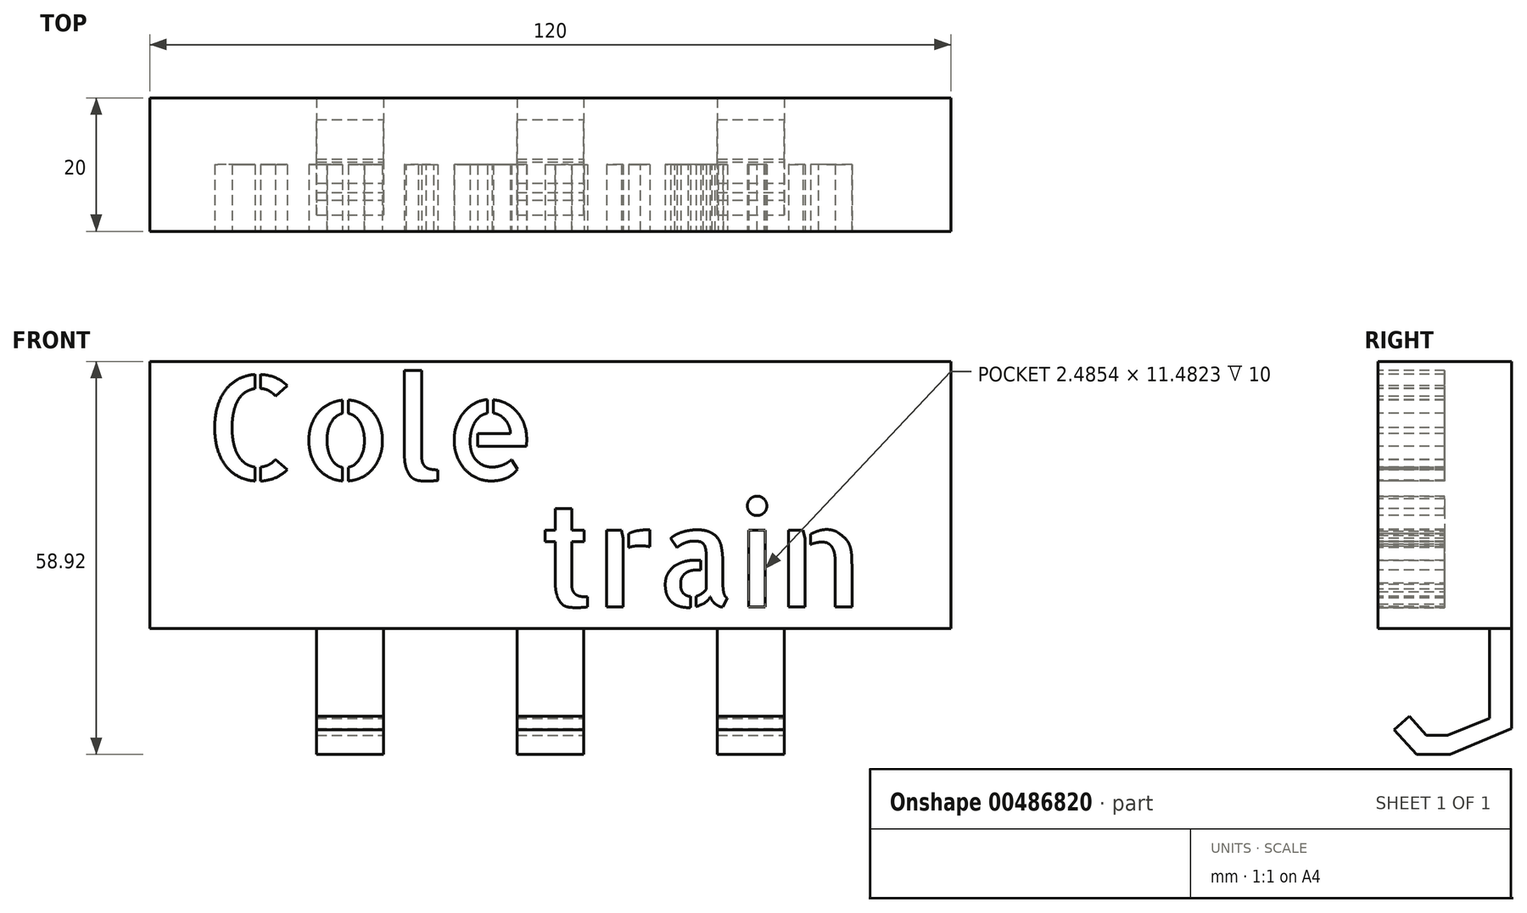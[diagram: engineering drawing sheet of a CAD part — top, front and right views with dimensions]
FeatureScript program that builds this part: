
annotation { "Feature Type Name" : "Feature", "Feature Type Description" : "" }
export const myFeature = defineFeature(function(context is Context, id is Id, definition is map)
    precondition{}
    {
        {
            var Q0;
            Q0=qCreatedBy(makeId("Front.planeOp"),FACE);
            var sketch = newSketch(context, id + "F0", { "sketchPlane" : qUnion([Q0])});
            skLineSegment(sketch, "E0", {"start": v(0, 0) * mm, "end": v(120, 0) * mm});
            skLineSegment(sketch, "E1", {"start": v(120, 0) * mm, "end": v(120, 40) * mm});
            skLineSegment(sketch, "E2", {"start": v(120, 40) * mm, "end": v(0, 40) * mm});
            skLineSegment(sketch, "E3", {"start": v(0, 40) * mm, "end": v(0, 0) * mm});
            skSolve(sketch);
        }
        {
            var Q0;
            Q0=makeQuery(id+"F0.imprint","IMPRINT",FACE,{"disambiguationData":[TD([[makeQuery(id+"F0.imprint","IMPRINT",EDGE,{"derivedFrom":sQuery(id+"F0.wireOp",EDGE,"E0")}),1.0]])]});
            extrude(context, id + "F1", {"entities" : qUnion([Q0]), "depth" : 20 * mm});
        }
        {
            var Q0;
            Q0=makeQuery(id+"FDrX07v6x76nU2d_1.boolean.opBoolean","MERGE",FACE,{"derivedFrom":[makeQuery(id+"F1.opExtrude","SWEPT_FACE",FACE,{"disambiguationData":[OSD([sQuery(id+"F0.wireOp",EDGE,"E3")])]}),makeQuery(id+"FDrX07v6x76nU2d_1.opExtrude","CAP_FACE",FACE,{"disambiguationData":[OSD([sQuery(id+"FK7LQfFWzsV9AYp_1.wireOp",EDGE,"OMKRaW7R-vSLb-FYLp-IFkI-dfkIP6oVdDYg"),sQuery(id+"FK7LQfFWzsV9AYp_1.wireOp",EDGE,"lYjhFyQz-pdgc-lFaZ-xAnS-GeXkMmyUxUMK"),sQuery(id+"FK7LQfFWzsV9AYp_1.wireOp",EDGE,"zUAezEfJ-fcOu-USHg-nBjk-tvtQ3sMSXvug"),sQuery(id+"FK7LQfFWzsV9AYp_1.wireOp",EDGE,"2Er81OVU-9qJa-L23g-iBGc-yoonpNpwCUbS"),sQuery(id+"FK7LQfFWzsV9AYp_1.wireOp",EDGE,"PpuGXbKU-hLP1-UUbL-IeXQ-y96dniKJ76El"),sQuery(id+"FK7LQfFWzsV9AYp_1.wireOp",EDGE,"mb6oPqYD-JF6T-TfRG-1Bwp-kSzYiZRObz3x"),sQuery(id+"FK7LQfFWzsV9AYp_1.wireOp",EDGE,"EnuxGocE-ggdU-0ooB-hZ5K-RwG9sS1lhak2"),sQuery(id+"FK7LQfFWzsV9AYp_1.wireOp",EDGE,"iuQDp4Cp-PRgE-UXjH-uZSU-5Cy1tqOp6oE6"),sQuery(id+"FK7LQfFWzsV9AYp_1.wireOp",EDGE,"NXjEv2nQ-JPso-gn4P-wQue-BciRGQNFK3fX"),sQuery(id+"FK7LQfFWzsV9AYp_1.wireOp",EDGE,"TtK5KWP1-CATt-S2zs-VjLP-lxPlcXjjFvsI")])],"isStart":true})]});
            cPlane(context, id + "F2", {"entities" : qUnion([Q0]), "cplaneType" : CPlaneType.OFFSET, "offset" : 30 * mm, "oppositeDirection" : true, "width" : 150 * mm, "height" : 150 * mm});
        }
        {
            var Q0;
            Q0=qCreatedBy(id+"F2.planeOp",FACE);
            var sketch = newSketch(context, id + "F3", { "sketchPlane" : qUnion([Q0])});
            skLineSegment(sketch, "E4.0.0", {"start": v(0, 40) * mm, "end": v(0, -15) * mm});
            skLineSegment(sketch, "E4.0.1", {"start": v(0, -15) * mm, "end": v(9.2, -18.92) * mm});
            skLineSegment(sketch, "E4.0.2", {"start": v(9.2, -18.92) * mm, "end": v(14.2, -18.92) * mm});
            skLineSegment(sketch, "E4.0.3", {"start": v(14.2, -18.92) * mm, "end": v(17.55, -15.21) * mm});
            skLineSegment(sketch, "E4.0.4", {"start": v(17.55, -15.21) * mm, "end": v(15.33, -13.2) * mm});
            skLineSegment(sketch, "E4.0.5", {"start": v(15.33, -13.2) * mm, "end": v(12.77, -16.03) * mm});
            skLineSegment(sketch, "E4.0.6", {"start": v(12.77, -16.03) * mm, "end": v(9.6, -16.03) * mm});
            skLineSegment(sketch, "E4.0.7", {"start": v(9.6, -16.03) * mm, "end": v(3.27, -13.5) * mm});
            skLineSegment(sketch, "E4.0.8", {"start": v(3.27, -13.5) * mm, "end": v(3.27, 0) * mm});
            skLineSegment(sketch, "E4.0.9", {"start": v(3.27, 0) * mm, "end": v(20, 0) * mm});
            skLineSegment(sketch, "E4.0.10", {"start": v(20, 0) * mm, "end": v(20, 40) * mm});
            skLineSegment(sketch, "E4.0.11", {"start": v(20, 40) * mm, "end": v(0, 40) * mm});
            skSolve(sketch);
        }
        {
            var Q0;
            Q0=makeQuery(id+"F3.imprint","IMPRINT",FACE,{"disambiguationData":[TD([[makeQuery(id+"F3.imprint","IMPRINT",EDGE,{"derivedFrom":sQuery(id+"F3.wireOp",EDGE,"E4.0.0")}),1.0]])]});
            extrude(context, id + "F4", {"entities" : qUnion([Q0]), "operationType" : NewBodyOperationType.ADD, "endBound" : BoundingType.SYMMETRIC, "depth" : 10 * mm});
        }
        {
            var Q0;
            Q0=qCreatedBy(id+"F2.planeOp",FACE);
            cPlane(context, id + "F5", {"entities" : qUnion([Q0]), "cplaneType" : CPlaneType.OFFSET, "offset" : 30 * mm, "oppositeDirection" : true, "width" : 150 * mm, "height" : 150 * mm});
        }
        {
            var Q0;
            Q0=qCreatedBy(id+"F5.planeOp",FACE);
            var sketch = newSketch(context, id + "F6", { "sketchPlane" : qUnion([Q0])});
            skLineSegment(sketch, "E5.0.0", {"start": v(0, 40) * mm, "end": v(0, -15) * mm});
            skLineSegment(sketch, "E5.0.1", {"start": v(0, -15) * mm, "end": v(9.2, -18.92) * mm});
            skLineSegment(sketch, "E5.0.2", {"start": v(9.2, -18.92) * mm, "end": v(14.2, -18.92) * mm});
            skLineSegment(sketch, "E5.0.3", {"start": v(14.2, -18.92) * mm, "end": v(17.55, -15.21) * mm});
            skLineSegment(sketch, "E5.0.4", {"start": v(17.55, -15.21) * mm, "end": v(15.33, -13.2) * mm});
            skLineSegment(sketch, "E5.0.5", {"start": v(15.33, -13.2) * mm, "end": v(12.77, -16.03) * mm});
            skLineSegment(sketch, "E5.0.6", {"start": v(12.77, -16.03) * mm, "end": v(9.6, -16.03) * mm});
            skLineSegment(sketch, "E5.0.7", {"start": v(9.6, -16.03) * mm, "end": v(3.27, -13.5) * mm});
            skLineSegment(sketch, "E5.0.8", {"start": v(3.27, -13.5) * mm, "end": v(3.27, 0) * mm});
            skLineSegment(sketch, "E5.0.9", {"start": v(3.27, 0) * mm, "end": v(20, 0) * mm});
            skLineSegment(sketch, "E5.0.10", {"start": v(20, 0) * mm, "end": v(20, 40) * mm});
            skLineSegment(sketch, "E5.0.11", {"start": v(20, 40) * mm, "end": v(0, 40) * mm});
            skSolve(sketch);
        }
        {
            var Q0;
            Q0 = qSketchRegion(id + "F6", true);
            extrude(context, id + "F7", {"entities" : qUnion([Q0]), "operationType" : NewBodyOperationType.ADD, "endBound" : BoundingType.SYMMETRIC, "depth" : 10 * mm});
        }
        {
            var Q0;
            Q0=qCreatedBy(id+"F5.planeOp",FACE);
            cPlane(context, id + "F8", {"entities" : qUnion([Q0]), "cplaneType" : CPlaneType.OFFSET, "offset" : 30 * mm, "oppositeDirection" : true, "width" : 150 * mm, "height" : 150 * mm});
        }
        {
            var Q0;
            Q0=qCreatedBy(id+"F8.planeOp",FACE);
            var sketch = newSketch(context, id + "F9", { "sketchPlane" : qUnion([Q0])});
            skLineSegment(sketch, "E6.0.0", {"start": v(0, 40) * mm, "end": v(0, -15) * mm});
            skLineSegment(sketch, "E6.0.1", {"start": v(0, -15) * mm, "end": v(9.2, -18.92) * mm});
            skLineSegment(sketch, "E6.0.2", {"start": v(9.2, -18.92) * mm, "end": v(14.2, -18.92) * mm});
            skLineSegment(sketch, "E6.0.3", {"start": v(14.2, -18.92) * mm, "end": v(17.55, -15.21) * mm});
            skLineSegment(sketch, "E6.0.4", {"start": v(17.55, -15.21) * mm, "end": v(15.33, -13.2) * mm});
            skLineSegment(sketch, "E6.0.5", {"start": v(15.33, -13.2) * mm, "end": v(12.77, -16.03) * mm});
            skLineSegment(sketch, "E6.0.6", {"start": v(12.77, -16.03) * mm, "end": v(9.6, -16.03) * mm});
            skLineSegment(sketch, "E6.0.7", {"start": v(9.6, -16.03) * mm, "end": v(3.27, -13.5) * mm});
            skLineSegment(sketch, "E6.0.8", {"start": v(3.27, -13.5) * mm, "end": v(3.27, 0) * mm});
            skLineSegment(sketch, "E6.0.9", {"start": v(3.27, 0) * mm, "end": v(20, 0) * mm});
            skLineSegment(sketch, "E6.0.10", {"start": v(20, 0) * mm, "end": v(20, 40) * mm});
            skLineSegment(sketch, "E6.0.11", {"start": v(20, 40) * mm, "end": v(0, 40) * mm});
            skSolve(sketch);
        }
        {
            var Q0;
            Q0 = qSketchRegion(id + "F9", true);
            extrude(context, id + "F10", {"entities" : qUnion([Q0]), "operationType" : NewBodyOperationType.ADD, "endBound" : BoundingType.SYMMETRIC, "depth" : 10 * mm});
        }
        {
            var Q0;
            Q0=makeQuery(id+"F1.opExtrude","CAP_FACE",FACE,{"disambiguationData":[OSD([sQuery(id+"F0.wireOp",EDGE,"E0"),sQuery(id+"F0.wireOp",EDGE,"E1"),sQuery(id+"F0.wireOp",EDGE,"E2"),sQuery(id+"F0.wireOp",EDGE,"E3")])],"isStart":false});
            var sketch = newSketch(context, id + "F11", { "sketchPlane" : qUnion([Q0])});
            skPoint(sketch, "E7.endSnap0", {"position": v(60, 0) * mm});
            skText(sketch, "E8", { "text": "Cole", "fontName": "AllertaStencil-Regular.ttf"});
            skText(sketch, "E9", { "text": "train", "fontName": "AllertaStencil-Regular.ttf"});
            const initialGuessF11  = {"E8": [0.00806, 0.02217, 1, 0, 0.01565], "E9": [0.05816, 0.0032, 1, 0, 0.01501]};
            skSetInitialGuess(sketch, initialGuessF11);
            skSolve(sketch);
        }
        {
            var Q0;
            Q0 = qSketchRegion(id + "F11", true);
            extrude(context, id + "F12", {"entities" : qUnion([Q0]), "operationType" : NewBodyOperationType.REMOVE, "oppositeDirection" : true, "depth" : 10 * mm});
        }
    });
